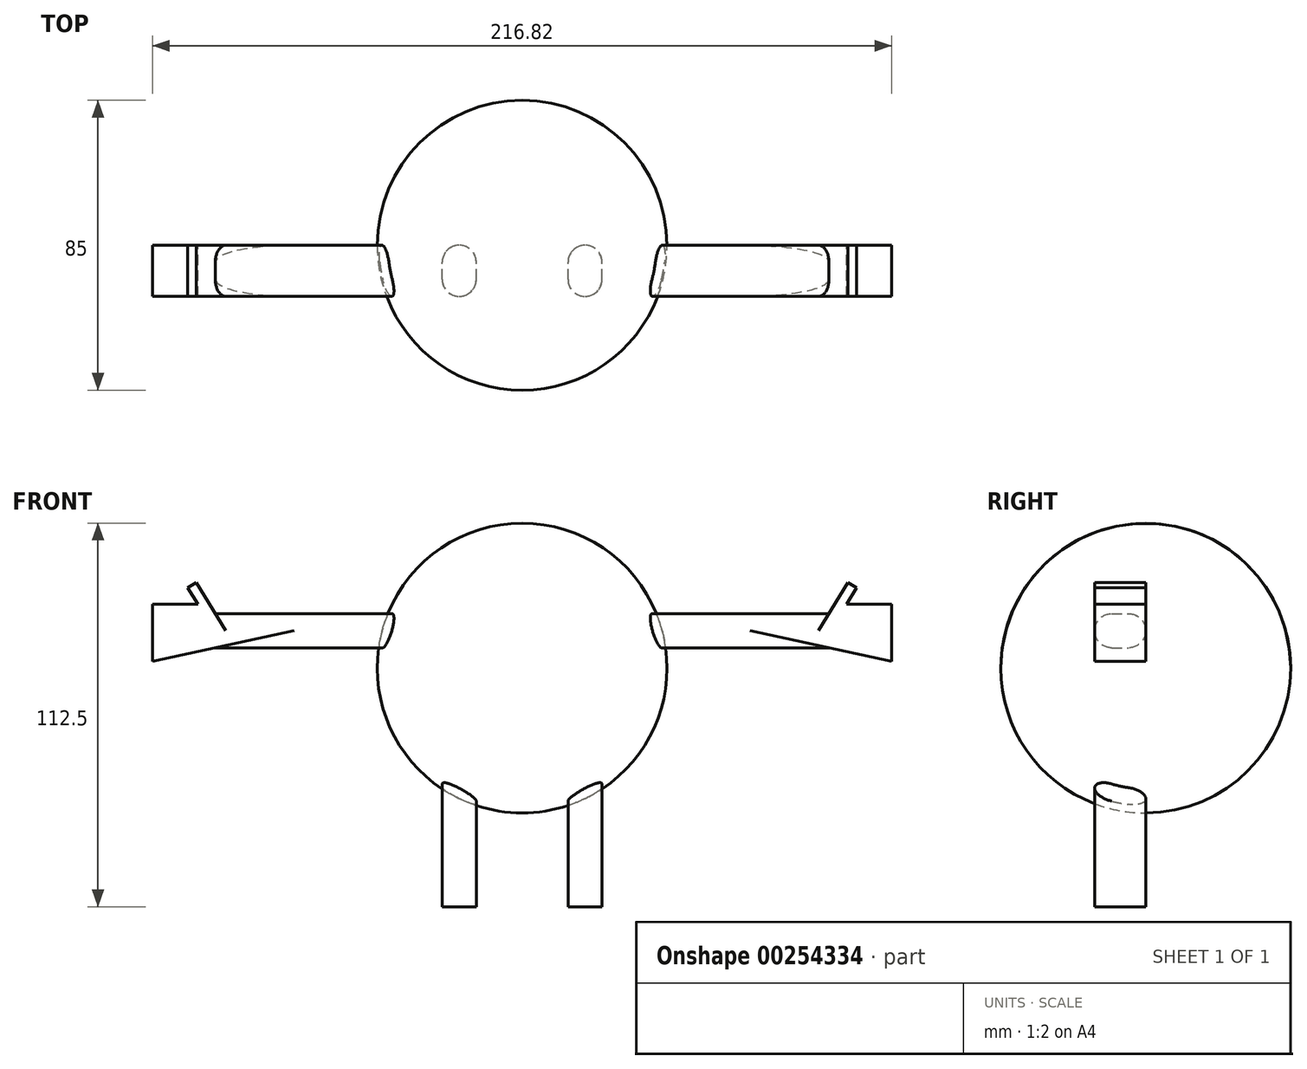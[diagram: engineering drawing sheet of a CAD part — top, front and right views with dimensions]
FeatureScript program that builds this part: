
annotation { "Feature Type Name" : "Feature", "Feature Type Description" : "" }
export const myFeature = defineFeature(function(context is Context, id is Id, definition is map)
    precondition{}
    {
        {
            var Q0;
            Q0=qCreatedBy(makeId("Front.planeOp"),FACE);
            var sketch = newSketch(context, id + "F0", { "sketchPlane" : qUnion([Q0])});
            skCircle(sketch, "E0", {"center": v(0, 0) * mm, "radius": 42.5 * mm});
            skLineSegment(sketch, "E1", {"start": v(-20.92, -37) * mm, "end": v(-20.92, -77.5) * mm, "construction": true});
            skLineSegment(sketch, "E2", {"start": v(0, 42.5) * mm, "end": v(-33.82, 42.5) * mm, "construction": true});
            skSolve(sketch);
        }
        {
            var Q0;
            Q0=makeQuery(id+"F0.imprint","IMPRINT",FACE,{"disambiguationData":[TD([[makeQuery(id+"F0.imprint","IMPRINT",EDGE,{"derivedFrom":sQuery(id+"F0.wireOp",EDGE,"E0")}),1.0]])]});
            extrude(context, id + "F1", {"entities" : qUnion([Q0]), "depth" : 85 / 2 * mm, "hasSecondDirection" : true, "secondDirectionOppositeDirection" : true, "secondDirectionDepth" : 42.5 * mm});
        }
        {
            var Q0;
            Q0=makeQuery(id+"F1.opExtrude","CAP_EDGE",EDGE,{"disambiguationData":[OSD([sQuery(id+"F0.wireOp",EDGE,"E0")])],"isStart":false});
            var Q1;
            Q1=makeQuery(id+"F1.opExtrude","CAP_EDGE",EDGE,{"disambiguationData":[OSD([sQuery(id+"F0.wireOp",EDGE,"E0")])],"isStart":true});
            fillet(context, id + "F2", {"entities" : qUnion([Q0, Q1]), "radius" : 42.5 * mm, "tangentPropagation" : true, "allowEdgeOverflow" : false});
        }
        {
            var Q0;
            Q0=qCreatedBy(makeId("Front.planeOp"),FACE);
            var sketch = newSketch(context, id + "F3", { "sketchPlane" : qUnion([Q0])});
            skLineSegment(sketch, "E3.bottom", {"start": v(-23.45, -23.82) * mm, "end": v(-13.45, -23.82) * mm});
            skLineSegment(sketch, "E3.top", {"start": v(-23.45, -70) * mm, "end": v(-13.45, -70) * mm});
            skLineSegment(sketch, "E3.left", {"start": v(-23.45, -23.82) * mm, "end": v(-23.45, -70) * mm});
            skLineSegment(sketch, "E3.right", {"start": v(-13.45, -23.82) * mm, "end": v(-13.45, -70) * mm});
            skLineSegment(sketch, "E4.MirrorCS", {"start": v(13.45, -23.82) * mm, "end": v(13.45, -70) * mm});
            skLineSegment(sketch, "E5.MirrorCS", {"start": v(23.45, -23.82) * mm, "end": v(23.45, -70) * mm});
            skLineSegment(sketch, "E6.MirrorCS", {"start": v(23.45, -23.82) * mm, "end": v(13.45, -23.82) * mm});
            skLineSegment(sketch, "E7.MirrorCS", {"start": v(23.45, -70) * mm, "end": v(13.45, -70) * mm});
            skLineSegment(sketch, "E8.bottom", {"start": v(-26.33, 15.94) * mm, "end": v(-90, 15.94) * mm});
            skLineSegment(sketch, "E8.top", {"start": v(-26.33, 5.94) * mm, "end": v(-90, 5.94) * mm});
            skLineSegment(sketch, "E8.left", {"start": v(-26.33, 15.94) * mm, "end": v(-26.33, 5.94) * mm});
            skLineSegment(sketch, "E9", {"start": v(-90, 15.94) * mm, "end": v(-95.6, 25.06) * mm});
            skLineSegment(sketch, "E10", {"start": v(-95.6, 25.06) * mm, "end": v(-98.07, 23.55) * mm});
            skLineSegment(sketch, "E11", {"start": v(-98.07, 23.55) * mm, "end": v(-95.1, 18.73) * mm});
            skLineSegment(sketch, "E12", {"start": v(-95.1, 18.73) * mm, "end": v(-108.41, 18.73) * mm});
            skLineSegment(sketch, "E13", {"start": v(-108.41, 18.73) * mm, "end": v(-108.41, 1.95) * mm});
            skLineSegment(sketch, "E14", {"start": v(-108.41, 1.95) * mm, "end": v(-90, 5.94) * mm});
            skLineSegment(sketch, "E15.MirrorCS", {"start": v(98.07, 23.55) * mm, "end": v(95.1, 18.73) * mm});
            skLineSegment(sketch, "E16.MirrorCS", {"start": v(95.6, 25.06) * mm, "end": v(98.07, 23.55) * mm});
            skLineSegment(sketch, "E17.MirrorCS", {"start": v(108.41, 1.95) * mm, "end": v(90, 5.94) * mm});
            skLineSegment(sketch, "E18.MirrorCS", {"start": v(26.33, 15.94) * mm, "end": v(90, 15.94) * mm});
            skLineSegment(sketch, "E19.MirrorCS", {"start": v(26.33, 5.94) * mm, "end": v(90, 5.94) * mm});
            skLineSegment(sketch, "E20.MirrorCS", {"start": v(108.41, 18.73) * mm, "end": v(108.41, 1.95) * mm});
            skLineSegment(sketch, "E21.MirrorCS", {"start": v(95.1, 18.73) * mm, "end": v(108.41, 18.73) * mm});
            skLineSegment(sketch, "E22.MirrorCS", {"start": v(26.33, 15.94) * mm, "end": v(26.33, 5.94) * mm});
            skLineSegment(sketch, "E23.MirrorCS", {"start": v(90, 15.94) * mm, "end": v(95.6, 25.06) * mm});
            skSolve(sketch);
        }
        {
            var Q0;
            Q0 = qSketchRegion(id + "F3", true);
            extrude(context, id + "F4", {"entities" : qUnion([Q0]), "operationType" : NewBodyOperationType.ADD, "depth" : 15 * mm});
        }
        {
            var Q0;
            Q0=makeQuery(id+"F4.opExtrude","CAP_EDGE",EDGE,{"disambiguationData":[OSD([sQuery(id+"F3.wireOp",EDGE,"E8.bottom")])],"isStart":false});
            var Q1;
            Q1=makeQuery(id+"F4.opExtrude","CAP_EDGE",EDGE,{"disambiguationData":[OSD([sQuery(id+"F3.wireOp",EDGE,"E8.top")])],"isStart":false});
            var Q2;
            Q2=makeQuery(id+"F4.opExtrude","CAP_EDGE",EDGE,{"disambiguationData":[OSD([sQuery(id+"F3.wireOp",EDGE,"E8.bottom")])],"isStart":true});
            var Q3;
            Q3=makeQuery(id+"F4.opExtrude","CAP_EDGE",EDGE,{"disambiguationData":[OSD([sQuery(id+"F3.wireOp",EDGE,"E18.MirrorCS")])],"isStart":true});
            var Q4;
            Q4=makeQuery(id+"F4.opExtrude","CAP_EDGE",EDGE,{"disambiguationData":[OSD([sQuery(id+"F3.wireOp",EDGE,"E18.MirrorCS")])],"isStart":false});
            var Q5;
            Q5=makeQuery(id+"F4.opExtrude","CAP_EDGE",EDGE,{"disambiguationData":[OSD([sQuery(id+"F3.wireOp",EDGE,"E19.MirrorCS")])],"isStart":false});
            var Q6;
            Q6=makeQuery(id+"F4.opExtrude","CAP_EDGE",EDGE,{"disambiguationData":[OSD([sQuery(id+"F3.wireOp",EDGE,"E5.MirrorCS")])],"isStart":false});
            var Q7;
            Q7=makeQuery(id+"F4.opExtrude","CAP_EDGE",EDGE,{"disambiguationData":[OSD([sQuery(id+"F3.wireOp",EDGE,"E4.MirrorCS")])],"isStart":false});
            var Q8;
            Q8=makeQuery(id+"F4.opExtrude","CAP_EDGE",EDGE,{"disambiguationData":[OSD([sQuery(id+"F3.wireOp",EDGE,"E3.right")])],"isStart":false});
            var Q9;
            Q9=makeQuery(id+"F4.opExtrude","CAP_EDGE",EDGE,{"disambiguationData":[OSD([sQuery(id+"F3.wireOp",EDGE,"E3.left")])],"isStart":false});
            var Q10;
            Q10=makeQuery(id+"F4.opExtrude","CAP_EDGE",EDGE,{"disambiguationData":[OSD([sQuery(id+"F3.wireOp",EDGE,"E3.right")])],"isStart":true});
            var Q11;
            Q11=makeQuery(id+"F4.opExtrude","CAP_EDGE",EDGE,{"disambiguationData":[OSD([sQuery(id+"F3.wireOp",EDGE,"E5.MirrorCS")])],"isStart":true});
            var Q12;
            Q12=makeQuery(id+"F4.opExtrude","CAP_EDGE",EDGE,{"disambiguationData":[OSD([sQuery(id+"F3.wireOp",EDGE,"E4.MirrorCS")])],"isStart":true});
            var Q13;
            Q13=makeQuery(id+"F4.opExtrude","CAP_EDGE",EDGE,{"disambiguationData":[OSD([sQuery(id+"F3.wireOp",EDGE,"E3.left")])],"isStart":true});
            var Q14;
            Q14=makeQuery(id+"F4.opExtrude","CAP_EDGE",EDGE,{"disambiguationData":[OSD([sQuery(id+"F3.wireOp",EDGE,"E19.MirrorCS")])],"isStart":true});
            var Q15;
            Q15=makeQuery(id+"F4.opExtrude","CAP_EDGE",EDGE,{"disambiguationData":[OSD([sQuery(id+"F3.wireOp",EDGE,"E8.top")])],"isStart":true});
            fillet(context, id + "F5", {"entities" : qUnion([Q0, Q1, Q2, Q3, Q4, Q5, Q6, Q7, Q8, Q9, Q10, Q11, Q12, Q13, Q14, Q15]), "radius" : 5 * mm, "tangentPropagation" : true, "allowEdgeOverflow" : false});
        }
    });
